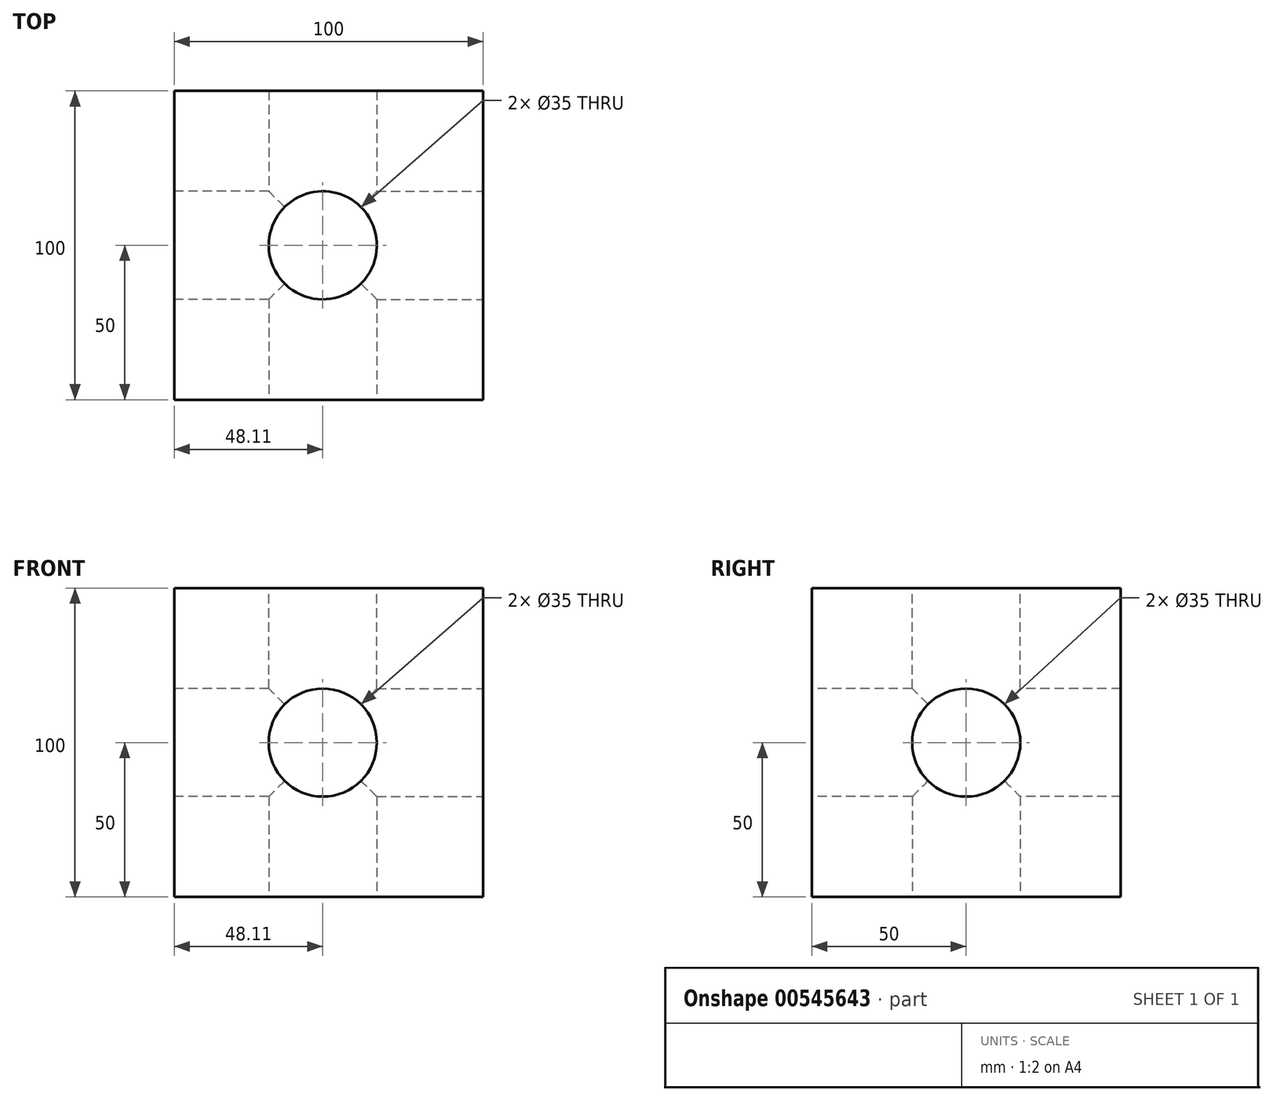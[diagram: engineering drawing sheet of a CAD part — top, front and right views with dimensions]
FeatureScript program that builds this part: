
annotation { "Feature Type Name" : "Feature", "Feature Type Description" : "" }
export const myFeature = defineFeature(function(context is Context, id is Id, definition is map)
    precondition{}
    {
        {
            var Q0;
            Q0=qCreatedBy(makeId("Front.planeOp"),FACE);
            var sketch = newSketch(context, id + "F0", { "sketchPlane" : qUnion([Q0])});
            skLineSegment(sketch, "E0.bottom", {"start": v(51.9, 50) * mm, "end": v(-48.1, 50) * mm});
            skLineSegment(sketch, "E0.top", {"start": v(51.9, -50) * mm, "end": v(-48.1, -50) * mm});
            skLineSegment(sketch, "E0.left", {"start": v(51.9, 50) * mm, "end": v(51.9, -50) * mm});
            skLineSegment(sketch, "E0.right", {"start": v(-48.1, 50) * mm, "end": v(-48.1, -50) * mm});
            skPoint(sketch, "E0.middle", {"position": v(1.9, 0) * mm});
            skSolve(sketch);
        }
        {
            var Q0;
            Q0 = qSketchRegion(id + "F0", true);
            extrude(context, id + "F1", {"entities" : qUnion([Q0]), "endBound" : BoundingType.SYMMETRIC, "depth" : 100 * mm, "offsetDistance" : 25 * mm});
        }
        {
            var Q0;
            Q0=qCreatedBy(makeId("Front.planeOp"),FACE);
            var sketch = newSketch(context, id + "F2", { "sketchPlane" : qUnion([Q0])});
            skCircle(sketch, "E1", {"center": v(0, 0) * mm, "radius": 17.5 * mm});
            skSolve(sketch);
        }
        {
            var Q0;
            Q0 = qSketchRegion(id + "F2", true);
            extrude(context, id + "F3", {"entities" : qUnion([Q0]), "operationType" : NewBodyOperationType.REMOVE, "endBound" : BoundingType.SYMMETRIC, "oppositeDirection" : true, "depth" : 100 * mm, "offsetDistance" : 25 * mm});
        }
        {
            var Q0;
            Q0=makeQuery(id+"F1.opExtrude","SWEPT_FACE",FACE,{"disambiguationData":[OSD([sQuery(id+"F0.wireOp",EDGE,"E0.left")])]});
            var sketch = newSketch(context, id + "F4", { "sketchPlane" : qUnion([Q0])});
            skCircle(sketch, "E2", {"center": v(0, 0) * mm, "radius": 17.5 * mm});
            skSolve(sketch);
        }
        {
            var Q0;
            Q0 = qSketchRegion(id + "F4", true);
            extrude(context, id + "F5", {"entities" : qUnion([Q0]), "operationType" : NewBodyOperationType.REMOVE, "endBound" : BoundingType.SYMMETRIC, "oppositeDirection" : true, "depth" : 100 * mm, "offsetDistance" : 25 * mm});
        }
        {
            var Q0;
            Q0=makeQuery(id+"F1.opExtrude","SWEPT_FACE",FACE,{"disambiguationData":[OSD([sQuery(id+"F0.wireOp",EDGE,"E0.right")])]});
            var sketch = newSketch(context, id + "F6", { "sketchPlane" : qUnion([Q0])});
            skCircle(sketch, "E3", {"center": v(0, 0) * mm, "radius": 17.5 * mm});
            skSolve(sketch);
        }
        {
            var Q0;
            Q0 = qSketchRegion(id + "F6", true);
            extrude(context, id + "F7", {"entities" : qUnion([Q0]), "operationType" : NewBodyOperationType.REMOVE, "endBound" : BoundingType.SYMMETRIC, "oppositeDirection" : true, "depth" : 100 * mm, "offsetDistance" : 25 * mm});
        }
        {
            var Q0;
            Q0=makeQuery(id+"F1.opExtrude","SWEPT_FACE",FACE,{"disambiguationData":[OSD([sQuery(id+"F0.wireOp",EDGE,"E0.bottom")])]});
            var sketch = newSketch(context, id + "F8", { "sketchPlane" : qUnion([Q0])});
            skCircle(sketch, "E4", {"center": v(0, 0) * mm, "radius": 17.5 * mm});
            skSolve(sketch);
        }
        {
            var Q0;
            Q0 = qSketchRegion(id + "F8", true);
            extrude(context, id + "F9", {"entities" : qUnion([Q0]), "operationType" : NewBodyOperationType.REMOVE, "endBound" : BoundingType.SYMMETRIC, "oppositeDirection" : true, "depth" : 100 * mm, "offsetDistance" : 25 * mm});
        }
        {
            var Q0;
            Q0=makeQuery(id+"F1.opExtrude","SWEPT_FACE",FACE,{"disambiguationData":[OSD([sQuery(id+"F0.wireOp",EDGE,"E0.top")])]});
            var sketch = newSketch(context, id + "F10", { "sketchPlane" : qUnion([Q0])});
            skCircle(sketch, "E5", {"center": v(0, 0) * mm, "radius": 17.5 * mm});
            skSolve(sketch);
        }
        {
            var Q0;
            Q0 = qSketchRegion(id + "F10", true);
            extrude(context, id + "F11", {"entities" : qUnion([Q0]), "operationType" : NewBodyOperationType.REMOVE, "endBound" : BoundingType.SYMMETRIC, "oppositeDirection" : true, "depth" : 100 * mm, "offsetDistance" : 25 * mm});
        }
    });
